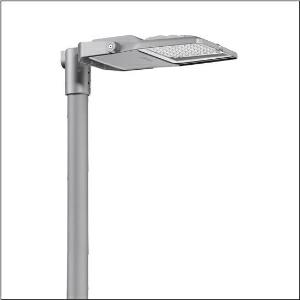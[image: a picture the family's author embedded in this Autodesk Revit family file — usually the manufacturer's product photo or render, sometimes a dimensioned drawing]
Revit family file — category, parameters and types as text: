
# Revit family: floodlight_fl_21_iq_mini___pl43_5xa7772c4a3a_a38e
name_source: partatom
category: Lighting Fixtures
units: mm (PartAtom-declared; Revit-internal decimal feet)

## family parameters
Cut with Voids When Loaded = No
Host = Face
Light Source = No
Part Type = Normal
Room Calculation Point = No
Round Connector Dimension = Use Diameter
Shared = No

## types (1)
- --- (1 x LED, 13050 lm, 87.2 W, 4000K)
    Apparent Load = 87 VA
    CIE Flux Codes = 27 78 99 100 100
    Color Rendering = 70
    Color Temperature = 4000K
    Default Elevation = 1800 mm
    Description = Floodlight FL 21 iQ mini, floodlight, primary light control with lens, of PMMA, primary optical cover: protective disc, of toughened safety glass, transparent, light distribution: PL43, light emission: direct distribution, installation type: surface-mounted, LED, High Power LED, rated luminous flux: 13.050lm, luminous efficacy: 150lm/W, light colour: 740, colour temperature: 4000K, control: Auto-Match, Temp-Guard, Night-Set, Smart-Wire, Desk-Remote (wireless, voltage-free reading and setting of iQ features in the workshop via application-optimized NFC function/RFID function), optimised constant luminous flux control (CLO 2.0), Light-Fading, Lumen-Switch, with terminal, 6-pole, mains connection: 220..240V, AC, 50/60Hz, start of lifetime: 87W, end of service life: 92W, reduction: 40W, luminaire housing, of diecast aluminium, powder-coated, Siteco® metallic grey (DB 702S), corrosivity category C5 mid according to DIN EN ISO 12944, sealing non-destructively replaceable, please order mast flange separately, mast bracket, of steel, galvanised, powder-coated, protection rating (complete): IP66, insulation class (complete): insulation class II (safety insulation), certification: CE, ENEC, VDE, protection symbol: D, impact resistance: IK08, permissible operating ambient temperature: -40..+40°C, permissible operating ambient temperature for outdoor applications: -40..+50°C, standard: DIN EN 12944, LABS conformity tested according to VDMA 24364:2018-05, packaging unit: 1 piece

Light Distribution: PL43
    Height = 70 mm
    Lamp = 1 x LED
    Lamp Light Flux = 13050 lm
    Lamp Power = 87.2 W
    Lamp count = 1
    Length = 485 mm
    Luminous efficacy = 150 lm/W
    Manufacturer = Siteco
    ModVariant = No
    Model = 5XA7772C4A3A
    Number of Poles = 1
    OnlyDefault = Yes
    Power Factor = 1
    Product Name = Floodlight FL 21 iQ mini | PL43
    Product group = floodlight | pylon annexe
    ProductGroupID = 6200
    Protection Class = Protection class II
    Protection Degree = IP 66
    RLX_Detail_Level = 1
    RLX_Emergency_Light_Flux = 0 lm
    RLX_Emergency_Type = 0
    RLX_Emergency_Type_DB = No
    RlxData = <blob elided: 101221 chars, md5=5046ac17>
    Socket = socket
    Standby Power = 0 W
    System Light Flux = 13050 lm
    System Power = 87 W
    Type Comments = factory setting: luminous flux: 100 % | dim-lin: 254 | 456 mA
    Type Image = l_1007125.jpg
    URL = http://relux.com
    VarID = @adj_112313
    Voltage = 0 V
    Weight = 0.00 kg
    Width = 337 mm

## geometry (parser evidence)
native form markers: Blend x4, Sweep x13
no freeform markers — native parametric forms only
